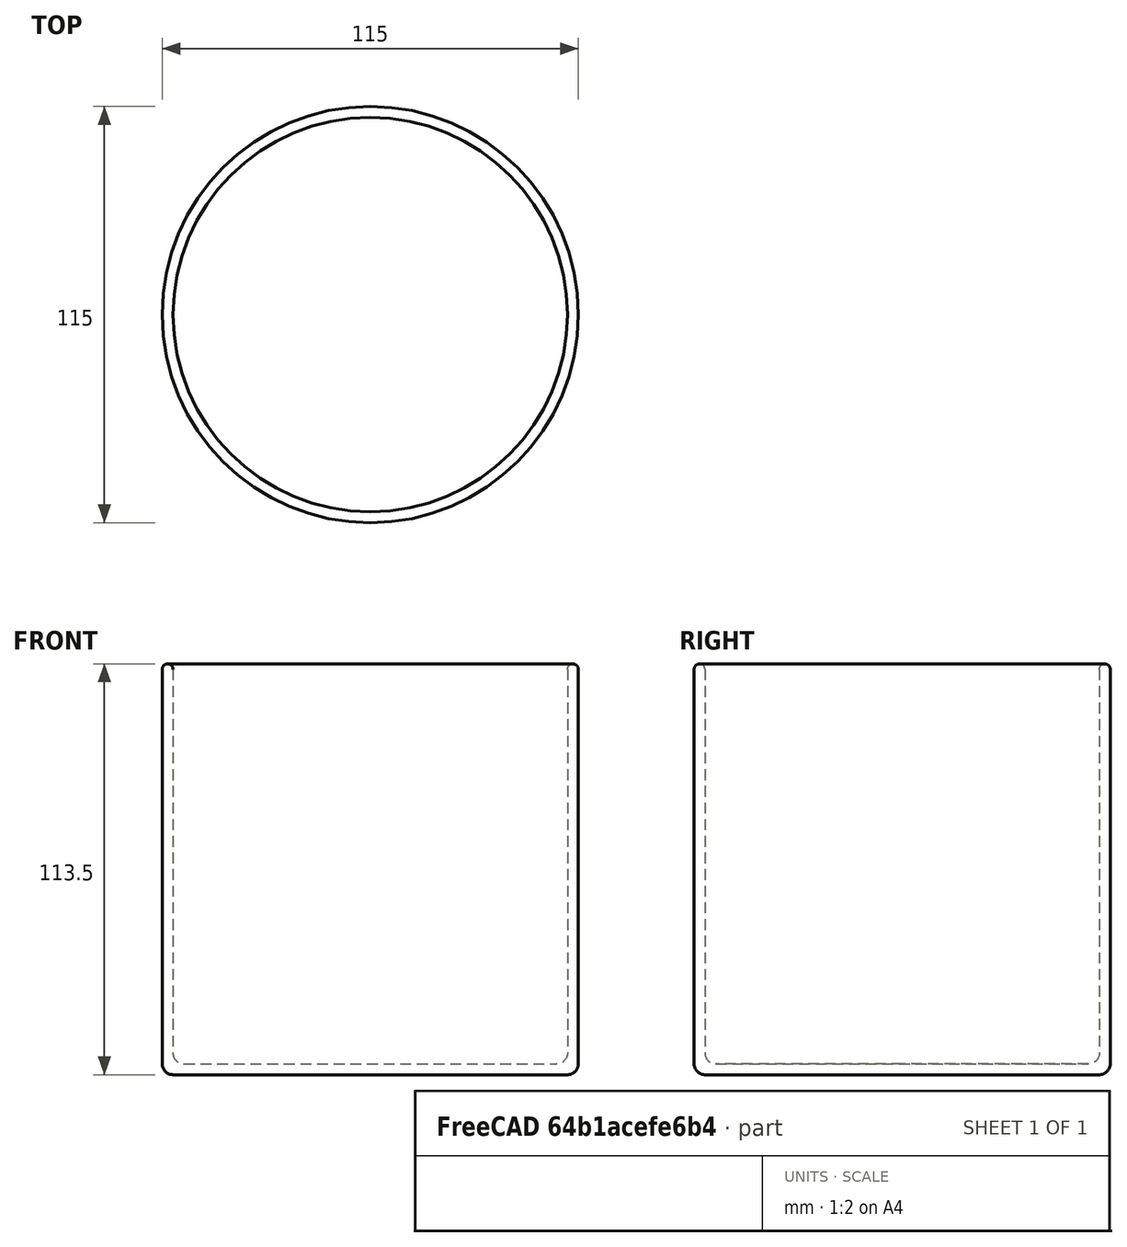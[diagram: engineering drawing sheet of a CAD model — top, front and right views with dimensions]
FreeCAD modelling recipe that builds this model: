
FCSTD DOCUMENT  (FreeCAD 1.0R39109 (Git))
Label: model
License: All rights reserved
LicenseURL: https://en.wikipedia.org/wiki/All_rights_reserved
objects: Sketcher::SketchObject×1, PartDesign::Revolution×1, PartDesign::Body×1
note: 6 computed .brp shape members not serialized (recipe doc carries the construction recipe); baked Part::Feature solids carry a one-line shape summary decoded from their .brp

FEATURE [Sketcher::SketchObject] Sketch
  ArcFitTolerance = 1e-06
  AttachmentSupport = -> [XZ_Plane]
  FullyConstrained = true
  MakeInternals = false
  MapMode = 5
  Placement = pos=(0,0,0) rot=(1,0,0;1.5708rad)
  expr: Constraints[17] = 115 / 2
  expr: Constraints[18] = 115 - 3
  sketch-geometry (10):
    g0: LineSegment StartX=-54.5 StartY=0 StartZ=0 EndX=0 EndY=0 EndZ=0
    g1: LineSegment StartX=-57.5 StartY=3 StartZ=0 EndX=-57.5 EndY=112 EndZ=0
    g2: ArcOfCircle CenterX=-56 CenterY=112 CenterZ=0 NormalX=0 NormalY=0 NormalZ=1 AngleXU=0 Radius=1.5 StartAngle=0 EndAngle=3.14159
    g3: LineSegment StartX=-54.5 StartY=112 StartZ=0 EndX=-54.5 EndY=6 EndZ=0
    g4: LineSegment StartX=0 StartY=3 StartZ=0 EndX=-51.5 EndY=3 EndZ=0
    g5: ArcOfCircle CenterX=-51.5 CenterY=6 CenterZ=0 NormalX=0 NormalY=0 NormalZ=1 AngleXU=0 Radius=3 StartAngle=3.14159 EndAngle=4.71239
    g6: GeomPoint [constr] X=-54.5 Y=3 Z=0
    g7: LineSegment StartX=0 StartY=3 StartZ=0 EndX=0 EndY=0 EndZ=0
    g8: ArcOfCircle CenterX=-54.5 CenterY=3 CenterZ=0 NormalX=0 NormalY=0 NormalZ=1 AngleXU=0 Radius=3 StartAngle=3.14159 EndAngle=4.71239
    g9: GeomPoint [constr] X=-57.5 Y=0 Z=0
  constraints (26):
    c: Horizontal(g0)
    c: Vertical(g1)
    c: Coincident(g2,g1)
    c: Horizontal(g1,g2)
    c: Horizontal(g2,g2)
    c: Radius(g2) = 1.5
    c: Coincident(g3,g2)
    c: Vertical(g3)
    c: PointOnObject(g4,g-2)
    c: Horizontal(g4)
    c: PointOnObject(g6,g4)
    c: PointOnObject(g6,g3)
    c: Tangent(g4,g5) = 1.5708
    c: Tangent(g3,g5) = -1.5708
    c: Radius(g5) = 3
    c: Coincident(g7,g4)
    c: Coincident(g7,g0)
    c: DistanceX(g9,g0) = 57.5
    c: DistanceY(g9,g1) = 112
    c: DistanceY(g7,g7) = 3
    c: Coincident(g0,g-1)
    c: PointOnObject(g9,g0)
    c: PointOnObject(g9,g1)
    c: Tangent(g0,g8) = -1.5708
    c: Tangent(g1,g8) = 1.5708
    c: Radius(g8) = 3
FEATURE [PartDesign::Revolution] Revolution
  Angle = 360
  Angle2 = 60
  Axis = (0,2e-16,1)
  Base = (0,0,0)
  Placement = pos=(0,0,0) rot=(1,0,0;1.5708rad)
  Profile = -> Sketch
  ReferenceAxis = -> Sketch [V_Axis]
  Refine = true
  Suppressed = false
  Type = 0
FEATURE [PartDesign::Body] Body
  AllowCompound = false
  Group = -> [Sketch,Revolution]
  Origin = -> Origin
  Tip = -> Revolution
